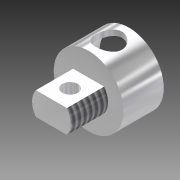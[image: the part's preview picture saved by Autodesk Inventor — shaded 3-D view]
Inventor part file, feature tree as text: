
AUTODESK INVENTOR PART (.ipt)
format: ipt  version: 2011 (Build 150239000, 239)  size: 130,048 bytes
history: native  units: in
note: dims shown in document units (in); Inventor stores cm internally (conversion verified against a paired STEP export)
features: extrude x5, sketch x5, thread x2, plane x1, projected_geometry x1
ambient origin geometry x8: Origin, YZ Plane, XZ Plane, XY Plane, X Axis, Y Axis, Z Axis, Center Point
bodies: Solid1 (feature_tree)
feature tree (14):
  extrude  "Extrusion1"  Depth=0.95in
  extrude  "Extrusion2"  Depth=0.1in TaperAngle=0.0deg
  extrude  "Extrusion3"  Depth=0.375in
  thread  "Thread1"  [1 undecoded]
  thread  "Thread2"  [1 undecoded]
  extrude  "Extrusion4"  Depth=1.0in TaperAngle=0.0deg
  plane  "Work Plane1"
  extrude  "Extrusion5"  Depth=0.25in
  sketch  "Sketch1"  dims[d0=1.125in d1=0.95in]
  sketch  "Sketch2"  dims[d2=0.55in d3=0.0in d4=0.1in d5=0.0in]
  sketch  "Sketch3"  dims[d6=0.625in d7=0.375in d8=0.0in d9=0.0in]
  sketch  "Sketch4"  dims[d10=0.6in d11=0.0in d12=1.0in d13=0.0in]
  sketch  "Sketch5"  dims[d14=1.0in d15=0.0in d16=0.25in d17=0.6in d18=0.0in d19=0.5625in d20=0.425in d21=0.6in d22=0.0in d23=0.325in d24=0.325in]
  projected_geometry  "Projected Loop1"
note: 2 required parameter values undecoded (feature->parameter linkage not recoverable at this tier; creation-order binding heuristic only, values carry confidence <= 0.55)
